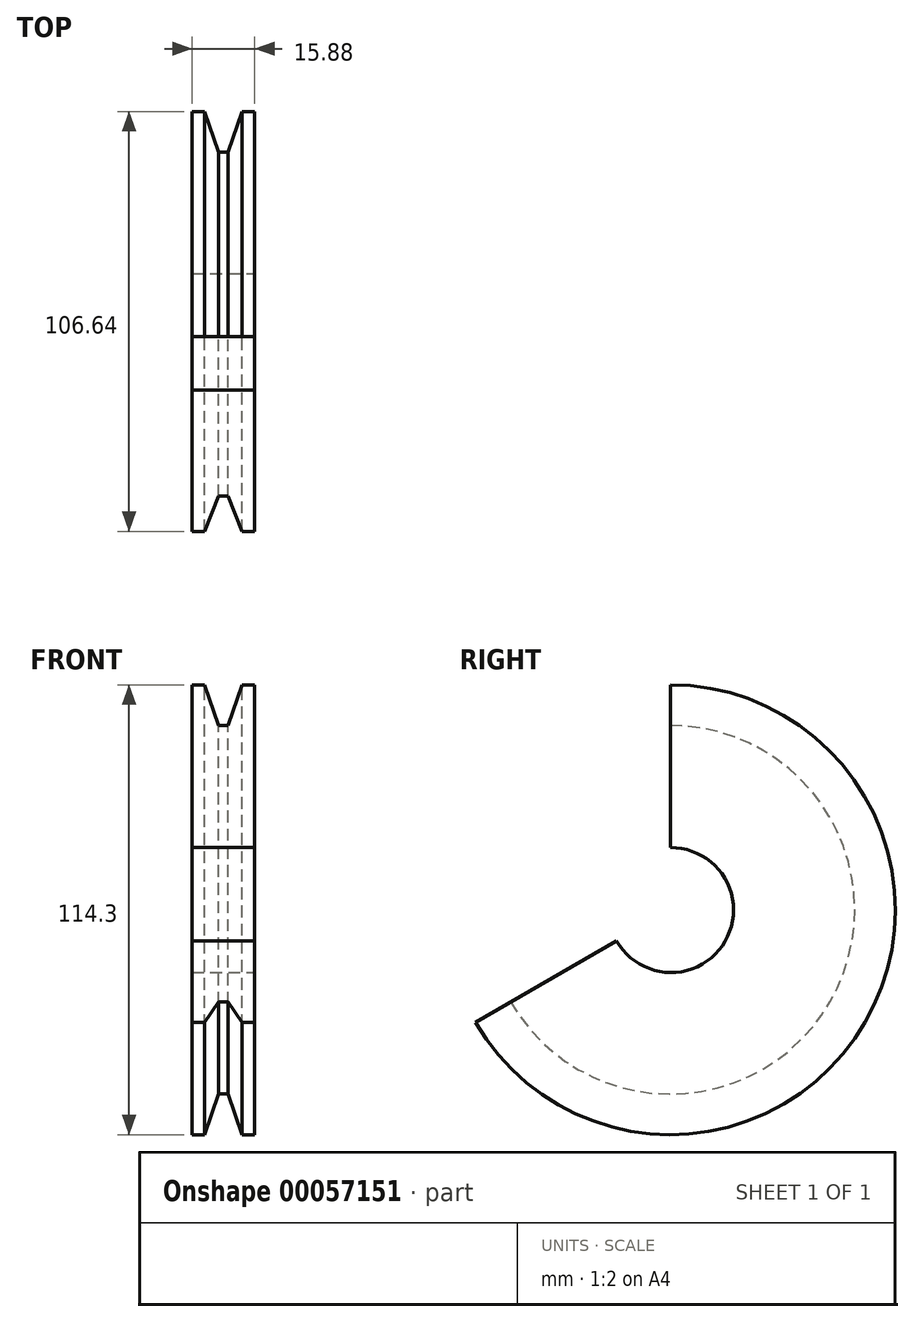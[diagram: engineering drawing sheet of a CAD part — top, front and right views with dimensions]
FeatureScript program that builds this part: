
annotation { "Feature Type Name" : "Feature", "Feature Type Description" : "" }
export const myFeature = defineFeature(function(context is Context, id is Id, definition is map)
    precondition{}
    {
        {
            var Q0;
            Q0=qCreatedBy(makeId("Front.planeOp"),FACE);
            var sketch = newSketch(context, id + "F0", { "sketchPlane" : qUnion([Q0])});
            skLineSegment(sketch, "E0", {"start": v(0, 0) * mm, "end": v(0, 57.15) * mm});
            skLineSegment(sketch, "E1", {"start": v(0, 57.15) * mm, "end": v(3.21, 57.15) * mm});
            skLineSegment(sketch, "E2", {"start": v(15.88, 57.15) * mm, "end": v(15.88, 0) * mm});
            skLineSegment(sketch, "E3", {"start": v(15.88, 0) * mm, "end": v(0, 0) * mm});
            skLineSegment(sketch, "E4.MirrorCS", {"start": v(0, 0) * mm, "end": v(0, -57.15) * mm});
            skLineSegment(sketch, "E5.MirrorCS", {"start": v(0, -57.15) * mm, "end": v(15.88, -57.15) * mm});
            skLineSegment(sketch, "E6.MirrorCS", {"start": v(15.87, -57.15) * mm, "end": v(15.87, 0) * mm});
            skLineSegment(sketch, "E7", {"start": v(3.21, 57.15) * mm, "end": v(6.76, 46.84) * mm});
            skLineSegment(sketch, "E8", {"start": v(6.76, 46.84) * mm, "end": v(9.11, 46.84) * mm});
            skLineSegment(sketch, "E9", {"start": v(9.11, 46.84) * mm, "end": v(12.66, 57.15) * mm});
            skLineSegment(sketch, "E10.trimOffspring", {"start": v(12.66, 57.15) * mm, "end": v(15.88, 57.15) * mm});
            skSolve(sketch);
        }
        {
            var Q0;
            Q0=makeQuery(id+"F0.imprint","IMPRINT",FACE,{"disambiguationData":[TD([[makeQuery(id+"F0.imprint","IMPRINT",EDGE,{"derivedFrom":sQuery(id+"F0.wireOp",EDGE,"E0")}),-1.0]])]});
            var Q1;
            Q1=sQuery(id+"F0.wireOp",EDGE,"E3");
            revolve(context, id + "F1", {"entities" : qUnion([Q0]), "axis" : qUnion([Q1]), "revolveType" : RevolveType.TWO_DIRECTIONS, "angle" : 240 * degree, "angleBack" : 360 * degree});
        }
        {
            var Q0;
            Q0=makeQuery(id+"F1.opRevolve","SWEPT_FACE",FACE,{"disambiguationData":[OSD([sQuery(id+"F0.wireOp",EDGE,"E2")])]});
            var sketch = newSketch(context, id + "F2", { "sketchPlane" : qUnion([Q0])});
            skCircle(sketch, "E11", {"center": v(0.16, -0.08) * mm, "radius": 15.88 * mm});
            skSolve(sketch);
        }
        {
            var Q0;
            Q0=sQuery(id+"F2.wireOp",VERTEX,"E11.center");
            var Q1;
            Q1=makeQuery(id+"F1.opRevolve","SWEPT_BODY",BODY,{"disambiguationData":[OSD([sQuery(id+"F0.wireOp",EDGE,"E0"),sQuery(id+"F0.wireOp",EDGE,"E1"),sQuery(id+"F0.wireOp",EDGE,"E2"),sQuery(id+"F0.wireOp",EDGE,"E3"),sQuery(id+"F0.wireOp",EDGE,"E7"),sQuery(id+"F0.wireOp",EDGE,"E8"),sQuery(id+"F0.wireOp",EDGE,"E9"),sQuery(id+"F0.wireOp",EDGE,"E10.trimOffspring")])]});
            hole(context, id + "F3", {"style" : HoleStyle.SIMPLE, "holeDiameter" : 31.75 * mm, "endStyle" : HoleEndStyle.THROUGH, "locations" : qUnion([Q0]), "scope" : qUnion([Q1])});
        }
    });
